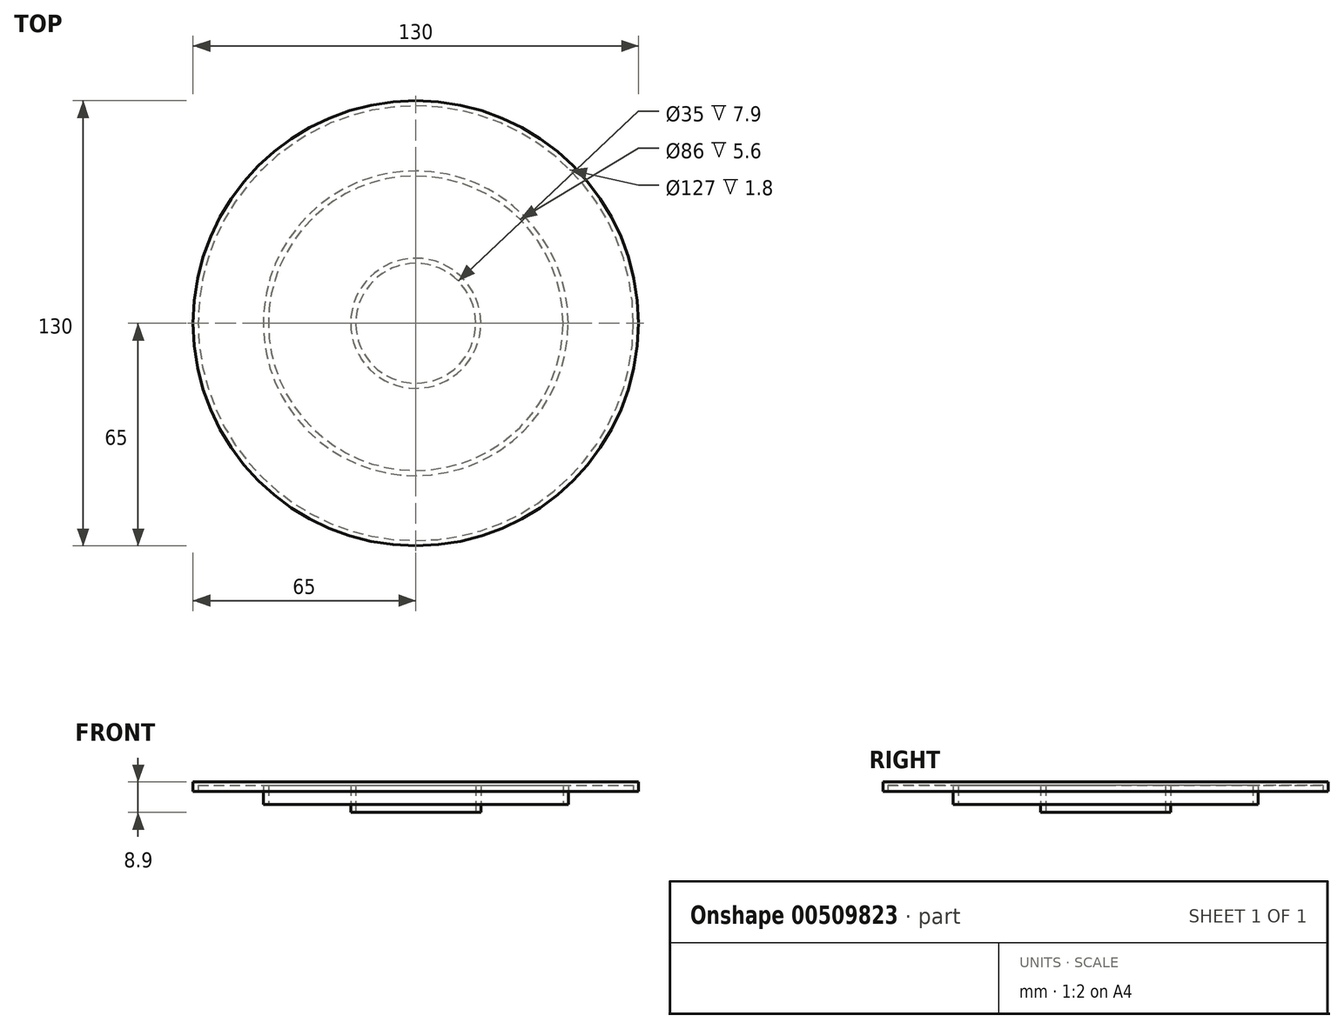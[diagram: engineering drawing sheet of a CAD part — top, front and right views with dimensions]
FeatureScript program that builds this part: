
annotation { "Feature Type Name" : "Feature", "Feature Type Description" : "" }
export const myFeature = defineFeature(function(context is Context, id is Id, definition is map)
    precondition{}
    {
        {
            var Q0;
            Q0=qCreatedBy(makeId("Front.planeOp"),FACE);
            var sketch = newSketch(context, id + "F0", { "sketchPlane" : qUnion([Q0])});
            skLineSegment(sketch, "E0", {"start": v(0, -6.5) * mm, "end": v(65, -6.5) * mm});
            skLineSegment(sketch, "E1.MirrorCS", {"start": v(65, -9.3) * mm, "end": v(63.5, -9.3) * mm});
            skLineSegment(sketch, "E2.MirrorCS", {"start": v(19, -15.41) * mm, "end": v(17.5, -15.41) * mm});
            skLineSegment(sketch, "E3.MirrorCS", {"start": v(44.5, -13.1) * mm, "end": v(43, -13.1) * mm});
            skLineSegment(sketch, "E4.MirrorCS", {"start": v(63.5, -9.3) * mm, "end": v(63.5, -7.5) * mm});
            skLineSegment(sketch, "E5.MirrorCS", {"start": v(0, -7.5) * mm, "end": v(0, -6.5) * mm});
            skLineSegment(sketch, "E6.MirrorCS", {"start": v(65, -6.51) * mm, "end": v(65, -9.3) * mm});
            skLineSegment(sketch, "E7.MirrorCS", {"start": v(43, -7.5) * mm, "end": v(19, -7.5) * mm});
            skLineSegment(sketch, "E8.MirrorCS", {"start": v(19, -7.5) * mm, "end": v(19, -15.4) * mm});
            skLineSegment(sketch, "E9.MirrorCS", {"start": v(17.5, -15.4) * mm, "end": v(17.5, -7.5) * mm});
            skLineSegment(sketch, "E10.MirrorCS", {"start": v(17.5, -7.51) * mm, "end": v(0, -7.5) * mm});
            skLineSegment(sketch, "E11.MirrorCS", {"start": v(43, -13.1) * mm, "end": v(43, -7.5) * mm});
            skLineSegment(sketch, "E12.MirrorCS", {"start": v(63.5, -7.5) * mm, "end": v(44.5, -7.5) * mm});
            skLineSegment(sketch, "E13.MirrorCS", {"start": v(44.5, -7.5) * mm, "end": v(44.5, -13.1) * mm});
            skSolve(sketch);
        }
        {
            var Q0;
            Q0=makeQuery(id+"F0.imprint","IMPRINT",FACE,{"disambiguationData":[TD([[makeQuery(id+"F0.imprint","IMPRINT",EDGE,{"derivedFrom":sQuery(id+"F0.wireOp",EDGE,"E1.MirrorCS")}),-1.0]])]});
            var Q1;
            Q1=sQuery(id+"F0.wireOp",EDGE,"E5.MirrorCS");
            revolve(context, id + "F1", {"entities" : qUnion([Q0]), "axis" : qUnion([Q1]), "revolveType" : RevolveType.FULL});
        }
    });
